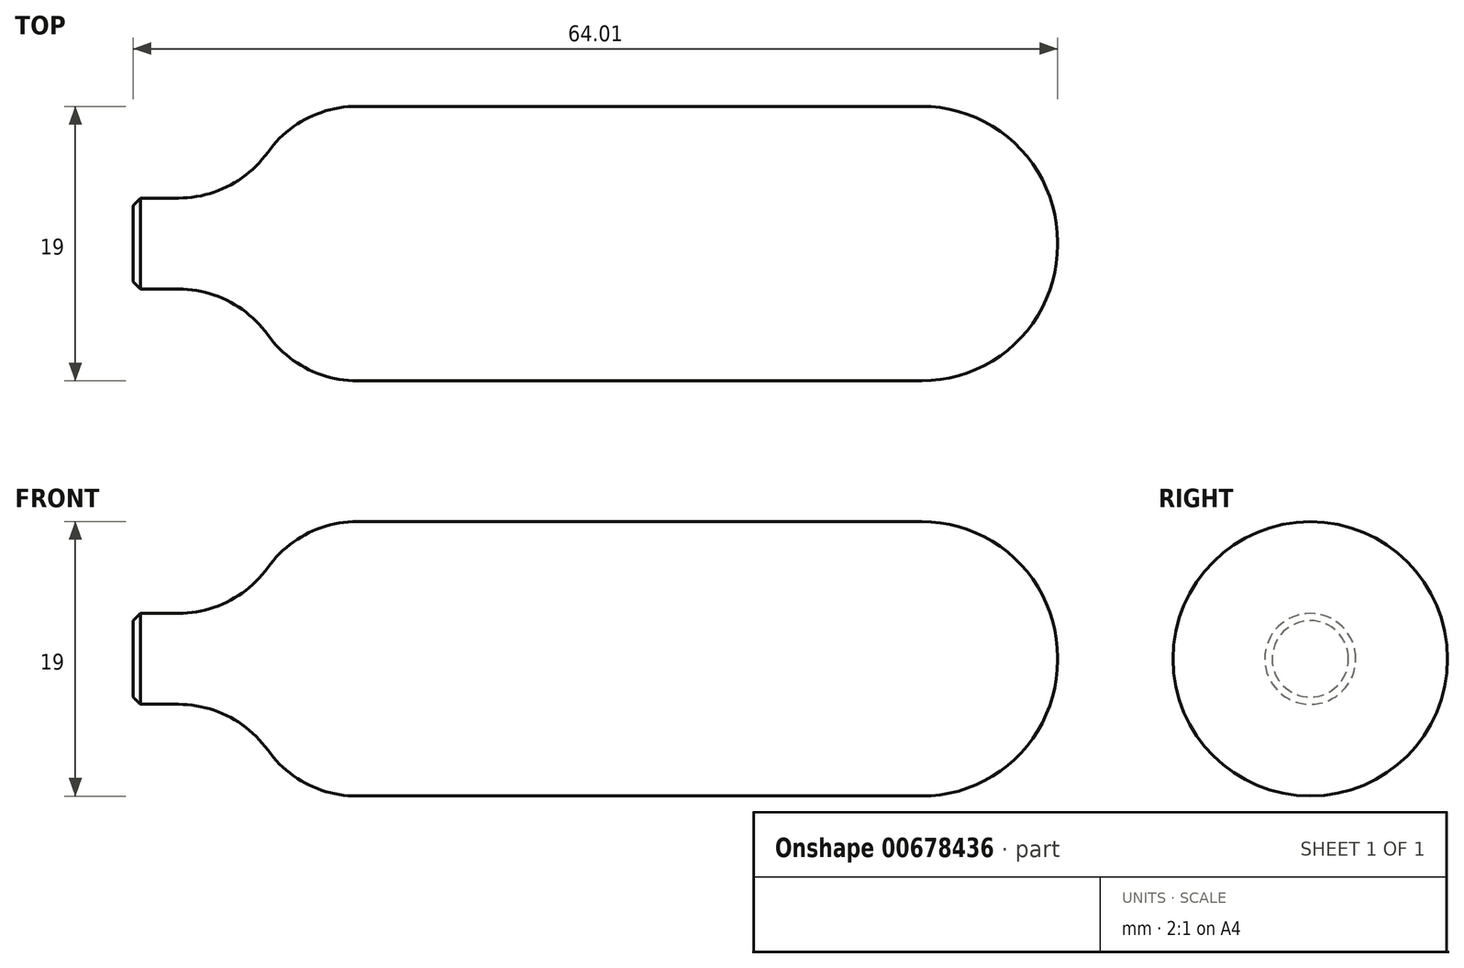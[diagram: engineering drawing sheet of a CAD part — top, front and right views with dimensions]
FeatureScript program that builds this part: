
annotation { "Feature Type Name" : "Feature", "Feature Type Description" : "" }
export const myFeature = defineFeature(function(context is Context, id is Id, definition is map)
    precondition{}
    {
        {
            var Q0;
            Q0=qCreatedBy(makeId("Front.planeOp"),FACE);
            var sketch = newSketch(context, id + "F0", { "sketchPlane" : qUnion([Q0])});
            skLineSegment(sketch, "E0.bottom", {"start": v(0, 0) * mm, "end": v(64, 0) * mm});
            skLineSegment(sketch, "E0.top", {"start": v(8, 9.5) * mm, "end": v(64, 9.5) * mm});
            skLineSegment(sketch, "E0.left", {"start": v(0, 0) * mm, "end": v(0, 3.15) * mm});
            skLineSegment(sketch, "E0.right", {"start": v(64, 0) * mm, "end": v(64, 9.5) * mm});
            skLineSegment(sketch, "E1.top", {"start": v(0, 3.15) * mm, "end": v(8, 3.15) * mm});
            skLineSegment(sketch, "E1.right", {"start": v(8, 9.5) * mm, "end": v(8, 3.15) * mm});
            skLineSegment(sketch, "E2", {"start": v(0, 0) * mm, "end": v(-9.06, 0) * mm});
            skSolve(sketch);
        }
        {
            var Q0;
            Q0=makeQuery(id+"F0.imprint","IMPRINT",FACE,{"disambiguationData":[TD([[makeQuery(id+"F0.imprint","IMPRINT",EDGE,{"derivedFrom":sQuery(id+"F0.wireOp",EDGE,"E0.bottom")}),1.0]])]});
            var Q1;
            Q1=sQuery(id+"F0.wireOp",EDGE,"E2");
            revolve(context, id + "F1", {"entities" : qUnion([Q0]), "axis" : qUnion([Q1]), "revolveType" : RevolveType.FULL});
        }
        {
            var Q0;
            Q0=makeQuery(id+"F1.opRevolve","SWEPT_EDGE",EDGE,{"disambiguationData":[OSD([sQuery(id+"F0.wireOp",EDGE,"E0.top"),sQuery(id+"F0.wireOp",EDGE,"E0.right")])]});
            fillet(context, id + "F2", {"entities" : qUnion([Q0]), "radius" : 9.4 * mm, "tangentPropagation" : true, "allowEdgeOverflow" : false});
        }
        {
            var Q0;
            Q0=makeQuery(id+"F1.opRevolve","SWEPT_EDGE",EDGE,{"disambiguationData":[OSD([sQuery(id+"F0.wireOp",EDGE,"E0.top"),sQuery(id+"F0.wireOp",EDGE,"E1.right")])]});
            fillet(context, id + "F3", {"entities" : qUnion([Q0]), "radius" : 7.62 * mm, "tangentPropagation" : true, "allowEdgeOverflow" : false});
        }
        {
            var Q0;
            Q0=makeQuery(id+"F3.opFillet","BLEND_EDGE",EDGE,{"blendedFrom":[makeQuery(id+"F1.opRevolve","SWEPT_EDGE",EDGE,{"disambiguationData":[OSD([sQuery(id+"F0.wireOp",EDGE,"E0.top"),sQuery(id+"F0.wireOp",EDGE,"E1.right")])]}),makeQuery(id+"F1.opRevolve","SWEPT_FACE",FACE,{"disambiguationData":[OSD([sQuery(id+"F0.wireOp",EDGE,"E1.top")])]})],"blendedInto":[makeQuery(id+"F1.opRevolve","SWEPT_FACE",FACE,{"disambiguationData":[OSD([sQuery(id+"F0.wireOp",EDGE,"E1.top")])]})]});
            fillet(context, id + "F4", {"entities" : qUnion([Q0]), "radius" : 7.62 * mm, "tangentPropagation" : true, "allowEdgeOverflow" : false});
        }
        {
            var Q0;
            Q0=makeQuery(id+"F1.opRevolve","SWEPT_EDGE",EDGE,{"disambiguationData":[OSD([sQuery(id+"F0.wireOp",EDGE,"E0.left"),sQuery(id+"F0.wireOp",EDGE,"E1.top")])]});
            chamfer(context, id + "F5", {"entities" : qUnion([Q0]), "width" : 0.5 * mm, "tangentPropagation" : true});
        }
    });
